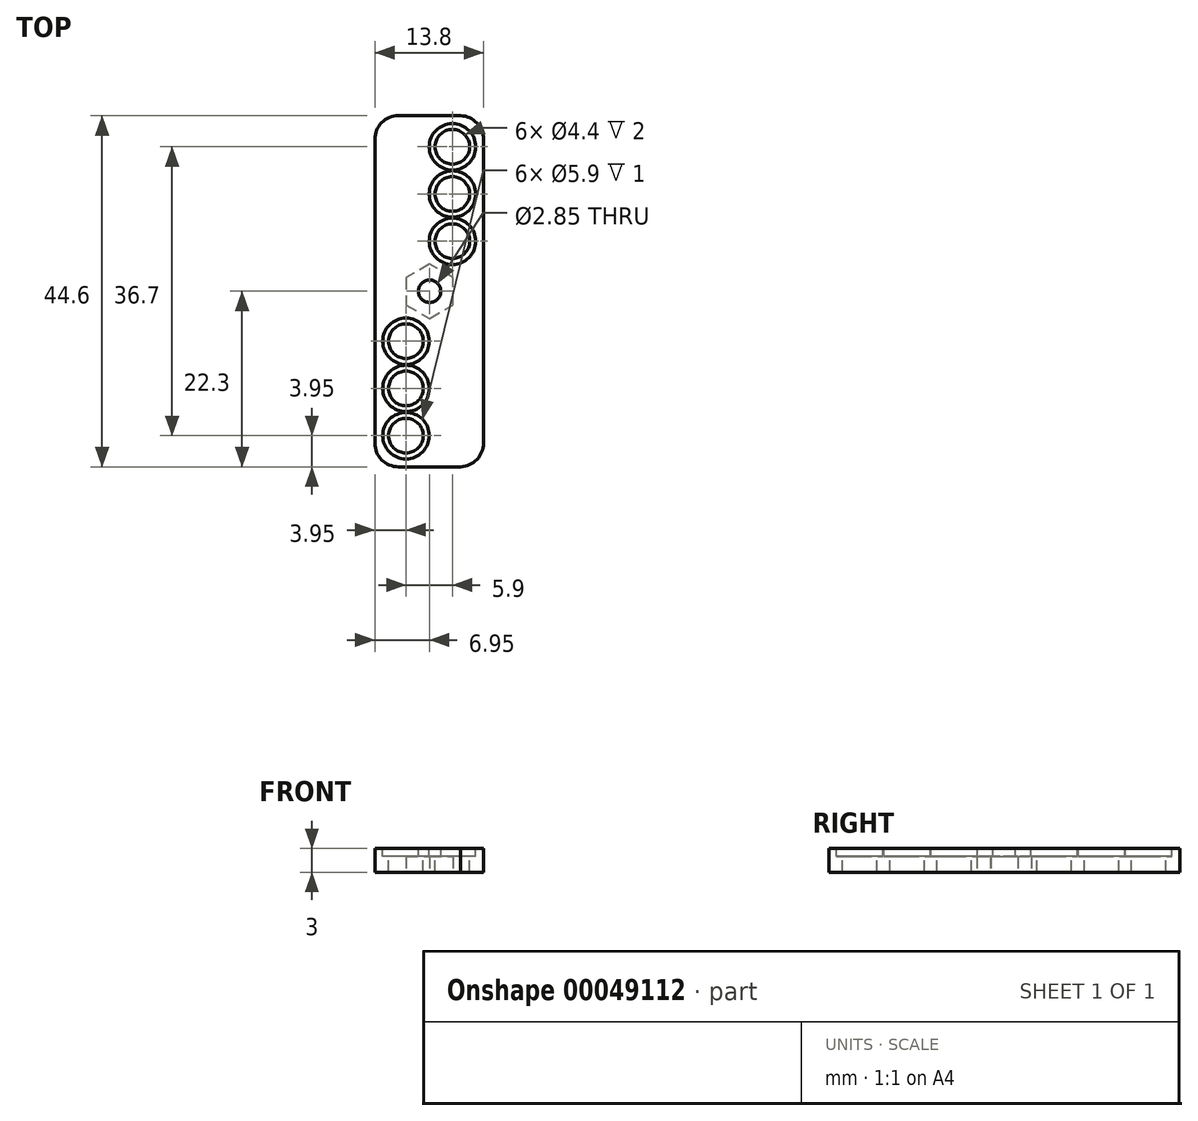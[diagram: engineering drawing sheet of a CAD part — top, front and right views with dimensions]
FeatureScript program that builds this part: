
annotation { "Feature Type Name" : "Feature", "Feature Type Description" : "" }
export const myFeature = defineFeature(function(context is Context, id is Id, definition is map)
    precondition{}
    {
        {
            var Q0;
            Q0=qCreatedBy(makeId("Top.planeOp"),FACE);
            var sketch = newSketch(context, id + "F0", { "sketchPlane" : qUnion([Q0])});
            skLineSegment(sketch, "E0", {"start": v(0, 0) * mm, "end": v(0, 22.3) * mm, "construction": true});
            skCircle(sketch, "E1", {"center": v(0, 18.35) * mm, "radius": 2.95 * mm});
            skPoint(sketch, "E2", {"position": v(0, 12.35) * mm});
            skCircle(sketch, "E3", {"center": v(0, 12.35) * mm, "radius": 2.95 * mm});
            skPoint(sketch, "E4", {"position": v(0, 6.35) * mm});
            skCircle(sketch, "E5", {"center": v(0, 6.35) * mm, "radius": 2.95 * mm});
            skLineSegment(sketch, "E6", {"start": v(0, 6.35) * mm, "end": v(-14.81, 6.35) * mm, "construction": true});
            skPoint(sketch, "E7", {"position": v(-6, 6.35) * mm});
            skCircle(sketch, "E8", {"center": v(-6, 6.35) * mm, "radius": 2.95 * mm, "construction": true});
            skPoint(sketch, "E9", {"position": v(-9.95, 6.35) * mm});
            skPoint(sketch, "E10.visualSharp", {"position": v(-9.85, 22.3) * mm});
            skCircle(sketch, "E11", {"center": v(0, 18.35) * mm, "radius": 2.2 * mm});
            skCircle(sketch, "E12", {"center": v(0, 12.35) * mm, "radius": 2.2 * mm});
            skCircle(sketch, "E13", {"center": v(0, 6.35) * mm, "radius": 2.2 * mm});
            skLineSegment(sketch, "E14", {"start": v(0, 6.35) * mm, "end": v(4.92, 6.35) * mm, "construction": true});
            skPoint(sketch, "E15", {"position": v(3.95, 6.35) * mm});
            skPoint(sketch, "E16", {"position": v(3.95, 0) * mm});
            skLineSegment(sketch, "E17", {"start": v(3.95, 0) * mm, "end": v(3.95, 19.3) * mm});
            skPoint(sketch, "E18.visualSharp", {"position": v(3.95, 22.3) * mm});
            skArc(sketch, "E18.filletArc", {"start": v(3.95, 19.3) * mm, "mid": v(3.1, 21.39) * mm, "end": v(1.05, 22.3) * mm});
            skArc(sketch, "E19.MirrorCS", {"start": v(3.95, -19.3) * mm, "mid": v(3.1, -21.39) * mm, "end": v(1.05, -22.3) * mm});
            skLineSegment(sketch, "E20.MirrorCS", {"start": v(3.95, 0) * mm, "end": v(3.95, -19.3) * mm});
            skLineSegment(sketch, "E21", {"start": v(1.05, 22.3) * mm, "end": v(-6.85, 22.3) * mm});
            skPoint(sketch, "E22", {"position": v(-9.85, 0) * mm});
            skLineSegment(sketch, "E23", {"start": v(-9.85, 0) * mm, "end": v(-9.85, 19.3) * mm});
            skArc(sketch, "E24.filletArc", {"start": v(-6.85, 22.3) * mm, "mid": v(-8.97, 21.42) * mm, "end": v(-9.85, 19.3) * mm});
            skLineSegment(sketch, "E25.MirrorCS", {"start": v(-9.85, 0) * mm, "end": v(-9.85, -19.3) * mm});
            skArc(sketch, "E26.MirrorCS", {"start": v(-6.85, -22.3) * mm, "mid": v(-8.97, -21.42) * mm, "end": v(-9.85, -19.3) * mm});
            skLineSegment(sketch, "E27.MirrorCS", {"start": v(1.05, -22.3) * mm, "end": v(-6.85, -22.3) * mm});
            skCircle(sketch, "E28.MirrorC", {"center": v(-5.9, -6.35) * mm, "radius": 2.95 * mm});
            skCircle(sketch, "E29.MirrorC", {"center": v(-5.9, -6.35) * mm, "radius": 2.2 * mm});
            skCircle(sketch, "E30.MirrorC", {"center": v(-5.9, -12.35) * mm, "radius": 2.95 * mm});
            skCircle(sketch, "E31.MirrorC", {"center": v(-5.9, -12.35) * mm, "radius": 2.2 * mm});
            skCircle(sketch, "E32.MirrorC", {"center": v(-5.9, -18.35) * mm, "radius": 2.95 * mm});
            skCircle(sketch, "E33.MirrorC", {"center": v(-5.9, -18.35) * mm, "radius": 2.2 * mm});
            skLineSegment(sketch, "E34", {"start": v(-2.9, 22.3) * mm, "end": v(-2.9, -22.3) * mm, "construction": true});
            skPoint(sketch, "E35", {"position": v(-2.9, 0) * mm});
            skCircle(sketch, "E36", {"center": v(-2.9, 0) * mm, "radius": 1.43 * mm});
            skCircle(sketch, "E37", {"center": v(-2.9, 0) * mm, "radius": 3 * mm, "construction": true});
            skLineSegment(sketch, "E38.0", {"start": v(0.12, -1.7) * mm, "end": v(-2.87, -3.46) * mm});
            skLineSegment(sketch, "E38.1", {"start": v(-2.87, -3.46) * mm, "end": v(-5.88, -1.76) * mm});
            skLineSegment(sketch, "E38.2", {"start": v(-5.88, -1.76) * mm, "end": v(-5.92, 1.7) * mm});
            skLineSegment(sketch, "E38.3", {"start": v(-5.92, 1.7) * mm, "end": v(-2.93, 3.46) * mm});
            skLineSegment(sketch, "E38.4", {"start": v(-2.93, 3.46) * mm, "end": v(0.08, 1.76) * mm});
            skLineSegment(sketch, "E38.5", {"start": v(0.08, 1.76) * mm, "end": v(0.12, -1.7) * mm});
            skPoint(sketch, "E38.0.midPoint", {"position": v(-1.37, -2.58) * mm});
            skSolve(sketch);
        }
        {
            var Q0;
            Q0=makeQuery(id+"F0.imprint","IMPRINT",FACE,{"disambiguationData":[TD([[makeQuery(id+"F0.imprint","IMPRINT",EDGE,{"derivedFrom":sQuery(id+"F0.wireOp",EDGE,"E1")}),-1.0]])]});
            var Q1;
            Q1=makeQuery(id+"F0.imprint","IMPRINT",FACE,{"disambiguationData":[TD([[makeQuery(id+"F0.imprint","IMPRINT",EDGE,{"derivedFrom":sQuery(id+"F0.wireOp",EDGE,"E1")}),1.0]])]});
            var Q2;
            Q2=makeQuery(id+"F0.imprint","IMPRINT",FACE,{"disambiguationData":[TD([[makeQuery(id+"F0.imprint","IMPRINT",EDGE,{"derivedFrom":sQuery(id+"F0.wireOp",EDGE,"E3")}),1.0]])]});
            var Q3;
            Q3=makeQuery(id+"F0.imprint","IMPRINT",FACE,{"disambiguationData":[TD([[makeQuery(id+"F0.imprint","IMPRINT",EDGE,{"derivedFrom":sQuery(id+"F0.wireOp",EDGE,"E36")}),-1.0]])]});
            var Q4;
            Q4=makeQuery(id+"F0.imprint","IMPRINT",FACE,{"disambiguationData":[TD([[makeQuery(id+"F0.imprint","IMPRINT",EDGE,{"derivedFrom":sQuery(id+"F0.wireOp",EDGE,"E28.MirrorC")}),1.0]])]});
            var Q5;
            Q5=makeQuery(id+"F0.imprint","IMPRINT",FACE,{"disambiguationData":[TD([[makeQuery(id+"F0.imprint","IMPRINT",EDGE,{"derivedFrom":sQuery(id+"F0.wireOp",EDGE,"E30.MirrorC")}),1.0]])]});
            var Q6;
            Q6=makeQuery(id+"F0.imprint","IMPRINT",FACE,{"disambiguationData":[TD([[makeQuery(id+"F0.imprint","IMPRINT",EDGE,{"derivedFrom":sQuery(id+"F0.wireOp",EDGE,"E32.MirrorC")}),1.0]])]});
            var Q7;
            Q7=makeQuery(id+"F0.imprint","IMPRINT",FACE,{"disambiguationData":[TD([[makeQuery(id+"F0.imprint","IMPRINT",EDGE,{"derivedFrom":sQuery(id+"F0.wireOp",EDGE,"E5")}),1.0]])]});
            extrude(context, id + "F1", {"entities" : qUnion([Q0, Q1, Q2, Q3, Q4, Q5, Q6, Q7]), "oppositeDirection" : true, "depth" : 3 * mm});
        }
        {
            var Q0;
            Q0=makeQuery(id+"F0.imprint","IMPRINT",FACE,{"disambiguationData":[TD([[makeQuery(id+"F0.imprint","IMPRINT",EDGE,{"derivedFrom":sQuery(id+"F0.wireOp",EDGE,"E28.MirrorC")}),1.0]])]});
            var Q1;
            Q1=makeQuery(id+"F0.imprint","IMPRINT",FACE,{"disambiguationData":[TD([[makeQuery(id+"F0.imprint","IMPRINT",EDGE,{"derivedFrom":sQuery(id+"F0.wireOp",EDGE,"E30.MirrorC")}),1.0]])]});
            var Q2;
            Q2=makeQuery(id+"F0.imprint","IMPRINT",FACE,{"disambiguationData":[TD([[makeQuery(id+"F0.imprint","IMPRINT",EDGE,{"derivedFrom":sQuery(id+"F0.wireOp",EDGE,"E32.MirrorC")}),1.0]])]});
            var Q3;
            Q3=makeQuery(id+"F0.imprint","IMPRINT",FACE,{"disambiguationData":[TD([[makeQuery(id+"F0.imprint","IMPRINT",EDGE,{"derivedFrom":sQuery(id+"F0.wireOp",EDGE,"E1")}),1.0]])]});
            var Q4;
            Q4=makeQuery(id+"F0.imprint","IMPRINT",FACE,{"disambiguationData":[TD([[makeQuery(id+"F0.imprint","IMPRINT",EDGE,{"derivedFrom":sQuery(id+"F0.wireOp",EDGE,"E3")}),1.0]])]});
            var Q5;
            Q5=makeQuery(id+"F0.imprint","IMPRINT",FACE,{"disambiguationData":[TD([[makeQuery(id+"F0.imprint","IMPRINT",EDGE,{"derivedFrom":sQuery(id+"F0.wireOp",EDGE,"E5")}),1.0]])]});
            extrude(context, id + "F2", {"entities" : qUnion([Q0, Q1, Q2, Q3, Q4, Q5]), "operationType" : NewBodyOperationType.REMOVE, "oppositeDirection" : true, "depth" : 1 * mm});
        }
        {
            var Q0;
            Q0=makeQuery(id+"F1.opExtrude","CAP_FACE",FACE,{"disambiguationData":[OSD([sQuery(id+"F0.wireOp",EDGE,"E11"),sQuery(id+"F0.wireOp",EDGE,"E12"),sQuery(id+"F0.wireOp",EDGE,"E13"),sQuery(id+"F0.wireOp",EDGE,"E17"),sQuery(id+"F0.wireOp",EDGE,"E18.filletArc"),sQuery(id+"F0.wireOp",EDGE,"E19.MirrorCS"),sQuery(id+"F0.wireOp",EDGE,"E20.MirrorCS"),sQuery(id+"F0.wireOp",EDGE,"E21"),sQuery(id+"F0.wireOp",EDGE,"E23"),sQuery(id+"F0.wireOp",EDGE,"E24.filletArc"),sQuery(id+"F0.wireOp",EDGE,"E25.MirrorCS"),sQuery(id+"F0.wireOp",EDGE,"E26.MirrorCS"),sQuery(id+"F0.wireOp",EDGE,"E27.MirrorCS"),sQuery(id+"F0.wireOp",EDGE,"E29.MirrorC"),sQuery(id+"F0.wireOp",EDGE,"E31.MirrorC"),sQuery(id+"F0.wireOp",EDGE,"E33.MirrorC"),sQuery(id+"F0.wireOp",EDGE,"E36")])],"isStart":false});
            var sketch = newSketch(context, id + "F3", { "sketchPlane" : qUnion([Q0])});
            skCircle(sketch, "E39", {"center": v(-2.9, 0) * mm, "radius": 3 * mm, "construction": true});
            skLineSegment(sketch, "E40.0", {"start": v(0.1, -1.72) * mm, "end": v(-2.9, -3.46) * mm});
            skLineSegment(sketch, "E40.1", {"start": v(-2.9, -3.46) * mm, "end": v(-5.9, -1.74) * mm});
            skLineSegment(sketch, "E40.2", {"start": v(-5.9, -1.74) * mm, "end": v(-5.9, 1.72) * mm});
            skLineSegment(sketch, "E40.3", {"start": v(-5.9, 1.72) * mm, "end": v(-2.9, 3.46) * mm});
            skLineSegment(sketch, "E40.4", {"start": v(-2.9, 3.46) * mm, "end": v(0.1, 1.74) * mm});
            skLineSegment(sketch, "E40.5", {"start": v(0.1, 1.74) * mm, "end": v(0.1, -1.72) * mm});
            skPoint(sketch, "E40.0.midPoint", {"position": v(-1.4, -2.6) * mm});
            skCircle(sketch, "E41", {"center": v(-2.9, 0) * mm, "radius": 1.43 * mm});
            skSolve(sketch);
        }
        {
            var Q0;
            Q0=makeQuery(id+"F3.imprint","IMPRINT",FACE,{"disambiguationData":[TD([[makeQuery(id+"F3.imprint","IMPRINT",EDGE,{"derivedFrom":sQuery(id+"F3.wireOp",EDGE,"E40.0")}),-1.0]])]});
            extrude(context, id + "F4", {"entities" : qUnion([Q0]), "operationType" : NewBodyOperationType.REMOVE, "oppositeDirection" : true, "depth" : 2 * mm});
        }
    });
